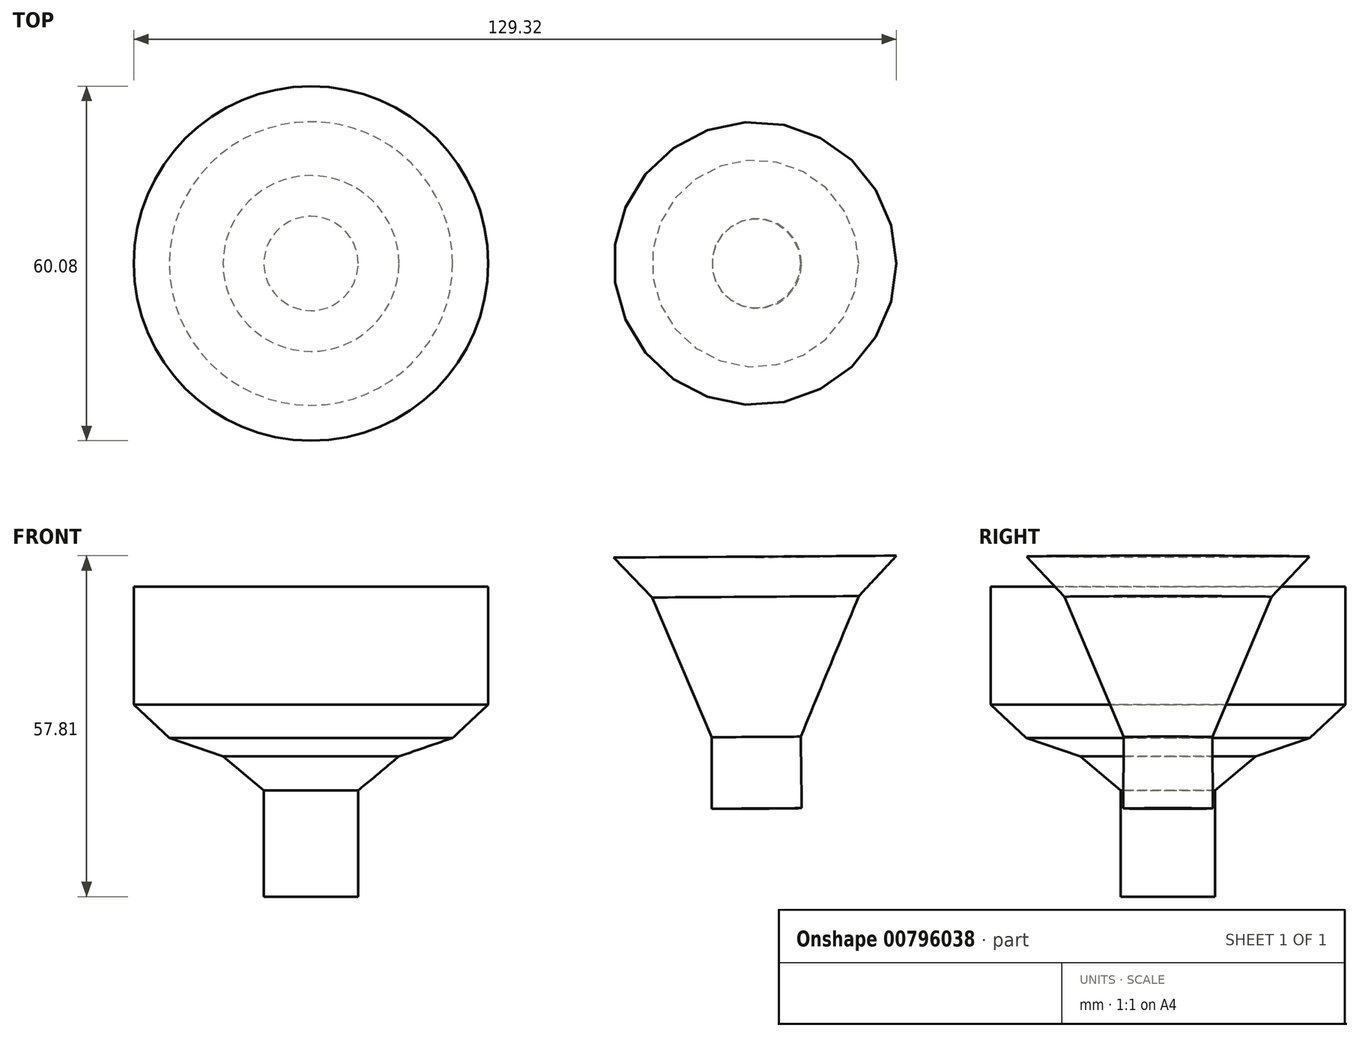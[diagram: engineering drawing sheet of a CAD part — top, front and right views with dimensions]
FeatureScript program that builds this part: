
annotation { "Feature Type Name" : "Feature", "Feature Type Description" : "" }
export const myFeature = defineFeature(function(context is Context, id is Id, definition is map)
    precondition{}
    {
        {
            var Q0;
            Q0=qCreatedBy(makeId("Front.planeOp"),FACE);
            var sketch = newSketch(context, id + "F0", { "sketchPlane" : qUnion([Q0])});
            skLineSegment(sketch, "E0", {"start": v(0, 37.66) * mm, "end": v(-30.04, 37.66) * mm});
            skLineSegment(sketch, "E1", {"start": v(-30.04, 37.66) * mm, "end": v(-30.04, 17.66) * mm});
            skLineSegment(sketch, "E2", {"start": v(-30.04, 17.66) * mm, "end": v(-24.03, 12.02) * mm});
            skLineSegment(sketch, "E3", {"start": v(-24.03, 12.02) * mm, "end": v(-14.9, 8.87) * mm});
            skLineSegment(sketch, "E4", {"start": v(-14.9, 8.87) * mm, "end": v(-8, 3.1) * mm});
            skLineSegment(sketch, "E5", {"start": v(-8, 3.1) * mm, "end": v(-8, -14.9) * mm});
            skLineSegment(sketch, "E6", {"start": v(-8, -14.9) * mm, "end": v(0, -14.9) * mm});
            skLineSegment(sketch, "E7", {"start": v(0, 37.66) * mm, "end": v(0, -14.9) * mm});
            skSolve(sketch);
        }
        {
            var Q0;
            Q0=makeQuery(id+"F0.imprint","IMPRINT",FACE,{"disambiguationData":[TD([[makeQuery(id+"F0.imprint","IMPRINT",EDGE,{"derivedFrom":sQuery(id+"F0.wireOp",EDGE,"E0")}),1.0]])]});
            var Q1;
            Q1=sQuery(id+"F0.wireOp",EDGE,"E7");
            revolve(context, id + "F1", {"surfaceOperationType" : NewSurfaceOperationType.NEW, "entities" : qUnion([Q0]), "axis" : qUnion([Q1]), "revolveType" : RevolveType.FULL});
        }
        {
            var Q0;
            Q0=qCreatedBy(makeId("Front.planeOp"),FACE);
            var sketch = newSketch(context, id + "F2", { "sketchPlane" : qUnion([Q0])});
            skLineSegment(sketch, "E8", {"start": v(75.59, 0) * mm, "end": v(67.97, 0) * mm});
            skLineSegment(sketch, "E9", {"start": v(67.97, 0) * mm, "end": v(67.97, 12.13) * mm});
            skLineSegment(sketch, "E10", {"start": v(67.97, 12.13) * mm, "end": v(57.82, 35.82) * mm});
            skLineSegment(sketch, "E11", {"start": v(57.82, 35.82) * mm, "end": v(51.33, 42.59) * mm});
            skLineSegment(sketch, "E12", {"start": v(51.33, 42.59) * mm, "end": v(75.3, 42.59) * mm});
            skLineSegment(sketch, "E13", {"start": v(75.3, 42.59) * mm, "end": v(75.59, 0) * mm});
            skSolve(sketch);
        }
        {
            var Q0;
            Q0=makeQuery(id+"F2.imprint","IMPRINT",FACE,{"disambiguationData":[TD([[makeQuery(id+"F2.imprint","IMPRINT",EDGE,{"derivedFrom":sQuery(id+"F2.wireOp",EDGE,"E8")}),-1.0]])]});
            var Q1;
            Q1=sQuery(id+"F2.wireOp",EDGE,"E13");
            revolve(context, id + "F3", {"surfaceOperationType" : NewSurfaceOperationType.NEW, "entities" : qUnion([Q0]), "axis" : qUnion([Q1]), "revolveType" : RevolveType.FULL});
        }
    });
